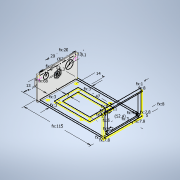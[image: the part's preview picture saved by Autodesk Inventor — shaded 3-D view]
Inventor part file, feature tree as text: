
AUTODESK INVENTOR PART (.ipt)
format: ipt  version: 2022 (Build 260153000, 153)  size: 899,584 bytes
history: native  units: mm
features: extrude x20, sketch x20, fillet x5, plane x4, projected_geometry x4, other x3, revolve x3, pattern_linear x1, mirror x1
ambient origin geometry x8: Origin, YZ Plane, XZ Plane, XY Plane, X Axis, Y Axis, Z Axis, Center Point
bodies: Solid1 (feature_tree)
feature tree (61):
  other  "pi_base_plane"
  extrude  "Extrusion1"  Depth=68.0mm
  extrude  "Extrusion2"  Depth=3.0mm
  other  "pi_outline"
  sketch  "Sketch4"  dims[d2=3.0mm d3=3.0mm]
  extrude  "Extrusion3"  Depth=3.0mm
  sketch  "Sketch5"  dims[d4=3.0mm d5=3.0mm]
  plane  "Work Plane1"
  revolve  "Revolution1"  [1 undecoded]
  sketch  "Sketch Driven Pattern1"  dims[d0=115.0mm d1=68.0mm]
  other  "door"
  extrude  "door_cut"  TaperAngle=0.0deg  [1 undecoded]
  extrude  "Extrusion5"  Depth=85.0mm
  sketch  "Sketch8"  dims[d8=38.0mm d9=0.0mm]
  plane  "Work Plane2"
  extrude  "Extrusion6"  Depth=3.5mm
  revolve  "Revolution2"  [1 undecoded]
  plane  "Work Plane3"
  revolve  "Revolution3"  [1 undecoded]
  fillet  "Fillet1"  Radius=2.7mm
  fillet  "Fillet2"  Radius=3.5mm
  extrude  "Extrusion7"  Depth=2.7mm
  extrude  "M2.5 Side Fastners"  Depth=58.0mm
  sketch  "Sketch14"  dims[d20=58.0mm d21=2.7mm]
  extrude  "Connector and Mount Holes"  Depth=3.0mm
  extrude  "Captive M6 Nut Indent"  Depth=6.5mm
  extrude  "Extrusion12"  Depth=6.5mm
  fillet  "Fillet3"  Radius=6.5mm
  sketch  "Sketch16"  dims[d24=62.0mm d25=3.0mm]
  extrude  "Extrusion13"  TaperAngle=0.0deg  [1 undecoded]
  extrude  "Extrusion14"  Depth=2.1mm
  extrude  "Extrusion15"  TaperAngle=90.0deg  [1 undecoded]
  extrude  "Extrusion16"  Depth=8.0mm
  fillet  "Fillet4"  Radius=8.0mm
  sketch  "Sketch19"  dims[d31=0.4mm d32=0.0mm]
  extrude  "Extrusion17"  Depth=5.0mm
  pattern_linear  "Rectangular Pattern1"  Spacing1=0.0mm  [1 undecoded]
  plane  "Work Plane4"
  mirror  "Mirror1"
  extrude  "Extrusion18"  Depth=2.0mm TaperAngle=0.0deg
  fillet  "Fillet6"  Radius=4.2mm
  extrude  "Extrusion19"  Depth=10.0mm
  extrude  "Extrusion20"  Depth=10.0mm
  extrude  "Extrusion21"  Depth=10.0mm
  projected_geometry  "Projected Loop1"
  sketch  "Sketch6"  dims[d6=3.0mm d7=0.0mm]
  sketch  "Sketch9"  dims[d10=56.0mm d11=85.0mm]
  sketch  "Sketch10"  dims[d12=2.7mm d13=3.5mm]
  projected_geometry  "Projected Loop2"
  sketch  "Sketch11"  dims[d14=3.5mm d15=2.7mm]
  projected_geometry  "Projected Loop3"
  sketch  "Sketch12"  dims[d16=3.5mm d17=3.5mm d18=2.7mm d19=3.5mm]
  sketch  "Sketch15"  dims[d22=3.5mm d23=58.0mm]
  sketch  "Sketch17"  dims[d26=4.0mm d27=6.5mm]
  sketch  "Sketch18"  dims[d28=6.5mm d29=6.5mm d30=6.5mm]
  projected_geometry  "Projected Loop4"
  sketch  "Sketch20"  dims[d34=4.2mm d35=2.1mm]
  sketch  "Sketch21"  dims[d36=14.3117mm d37=90.0deg]
  sketch  "Sketch22"  dims[d38=8.0mm d39=8.0mm d40=8.0mm]
  sketch  "Sketch23"  dims[d41=5.0mm d42=5.0mm]
  sketch  "Sketch24"  dims[d43=3.0mm d44=0.0mm d45=2.0mm d46=0.0mm d47=4.2mm d48=7.8mm d49=7.8mm d50=4.2mm d51=7.8mm d52=7.8mm d53=3.0mm d54=0.0mm d55=14.3117mm d56=90.0deg d57=52.4mm d58=14.3117mm d59=90.0deg d60=1.0mm d61=1.0mm d62=1.0mm d63=1.0mm d64=0.0mm d65=1.9mm d66=3.0mm d67=0.0mm d70=2.65mm d71=2.65mm d72=20.0mm d73=80.0mm d75=8.0mm d76=0.0mm d77=0.0mm d78=6.3mm d79=9.0mm d80=13.0mm d81=6.0mm d82=9.1mm d84=62.0mm d85=31.0mm d88=0.0mm d89=0.0mm d90=11.0mm d91=2.0mm d92=0.0mm d93=13.0mm d94=20.0mm d95=20.0mm d96=68.0mm d97=58.5mm d98=2.5mm d99=2.5mm d100=2.25mm d101=11.0mm d102=11.0mm d103=6.3mm d104=4.65mm d105=4.65mm d106=5.0mm d107=0.0mm d108=5.0mm d109=47.0mm d110=27.0mm d111=14.0mm d112=11.0mm d113=7.0mm d114=0.0mm d115=0.0mm d116=2.0mm d117=0.0mm d118=3.15mm d119=7.0mm d122=3.15mm d125=3.15mm d128=3.15mm d131=0.0mm d132=0.0mm d133=1.5mm d134=1.0mm d135=0.0mm d136=0.5mm d137=11.0mm d138=5.5mm d139=13.0mm d140=4.0mm d141=1.1mm d142=0.0mm d143=20.0mm d145=80.0mm d147=31.0mm d148=31.0mm d149=51.0mm d150=0.0mm d151=15.5mm d152=25.5mm d153=6.0mm d154=37.0mm d155=57.0mm d156=25.0mm d157=20.0mm d158=1.1mm d159=0.0mm d160=2.0mm d161=0.0mm d162=0.0mm d163=0.0mm d164=1.0mm d165=0.0mm d166=2.0mm d167=2.0mm d168=10.0mm d169=0.0mm]
note: 7 required parameter values undecoded (feature->parameter linkage not recoverable at this tier; creation-order binding heuristic only, values carry confidence <= 0.55)